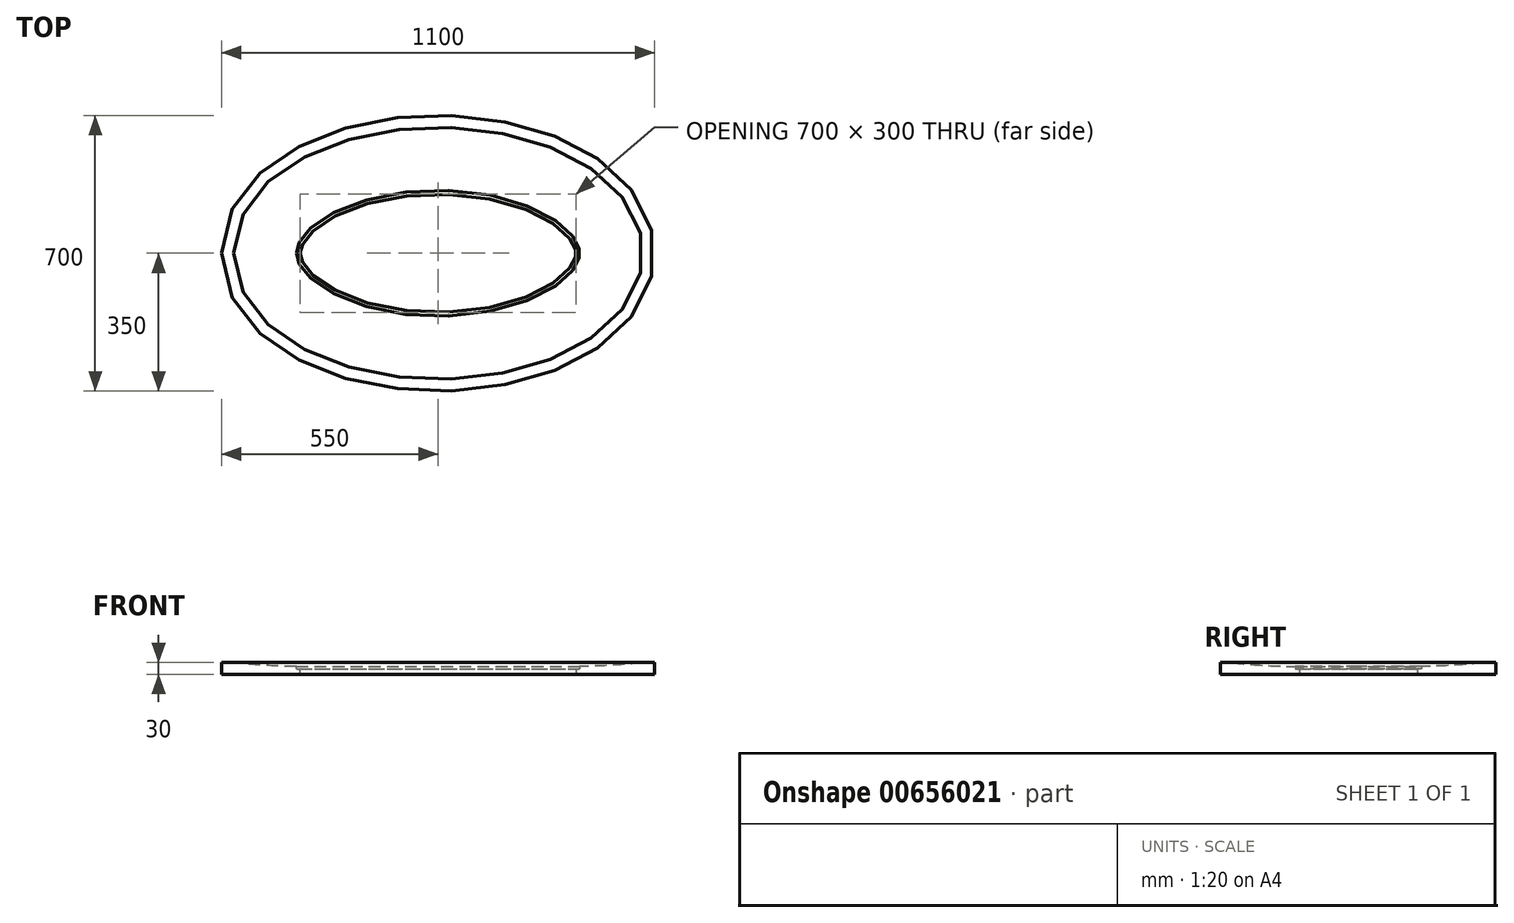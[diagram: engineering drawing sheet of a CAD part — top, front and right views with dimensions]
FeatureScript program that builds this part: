
annotation { "Feature Type Name" : "Feature", "Feature Type Description" : "" }
export const myFeature = defineFeature(function(context is Context, id is Id, definition is map)
    precondition{}
    {
        {
            var Q0;
            Q0=qCreatedBy(makeId("Top.planeOp"),FACE);
            var sketch = newSketch(context, id + "F0", { "sketchPlane" : qUnion([Q0])});
            skLineSegment(sketch, "E0", {"start": v(0, 0) * mm, "end": v(900, 0) * mm, "construction": true});
            skPoint(sketch, "E1", {"position": v(450, 0) * mm});
            skEllipse(sketch, "E2", {"center": v(450, 0) * mm, "majorRadius": 450 * mm, "minorRadius": 250 * mm, "majorAxis": v(-1, 0)});
            skSolve(sketch);
        }
        {
            var Q0;
            Q0=qCreatedBy(makeId("Front.planeOp"),FACE);
            var sketch = newSketch(context, id + "F1", { "sketchPlane" : qUnion([Q0])});
            skLineSegment(sketch, "E3.top", {"start": v(-100, -15) * mm, "end": v(100, -15) * mm});
            skLineSegment(sketch, "E3.left", {"start": v(-100, 15) * mm, "end": v(-100, -15) * mm});
            skLineSegment(sketch, "E3.right", {"start": v(100, -1) * mm, "end": v(100, -15) * mm});
            skLineSegment(sketch, "E4", {"start": v(100, -1) * mm, "end": v(90, -1) * mm});
            skLineSegment(sketch, "E5", {"start": v(90, -1) * mm, "end": v(90, 5) * mm});
            skLineSegment(sketch, "E6", {"start": v(-100, 15) * mm, "end": v(-70, 15) * mm});
            skArc(sketch, "E7", {"start": v(-70, 15) * mm, "mid": v(9.88, 8) * mm, "end": v(90, 5) * mm});
            skSolve(sketch);
        }
        {
            var Q0;
            Q0=qSketchRegion(id+"F1",true);
            var Q1;
            Q1=sQuery(id+"F0.wireOp",EDGE,"E2");
            sweep(context, id + "F2", {"profiles" : qUnion([Q0]), "path" : qUnion([Q1])});
        }
    });
